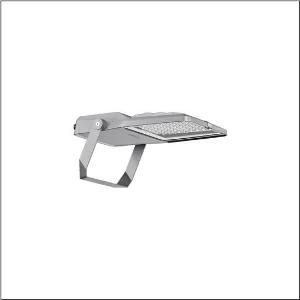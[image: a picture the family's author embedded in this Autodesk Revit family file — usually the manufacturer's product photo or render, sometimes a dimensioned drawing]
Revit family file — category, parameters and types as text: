
# Revit family: floodlight_fl_21_mini___pl64_5xa7775d2e1a_23e2
name_source: partatom
category: Lighting Fixtures
units: mm (PartAtom-declared; Revit-internal decimal feet)

## family parameters
Cut with Voids When Loaded = No
Host = Face
Light Source = No
Part Type = Normal
Room Calculation Point = No
Round Connector Dimension = Use Diameter
Shared = No

## types (1)
- --- (1 x LED, 17220 lm, 142.9 W, 3000K)
    Apparent Load = 143 VA
    CIE Flux Codes = 28 80 98 100 100
    Color Rendering = 70
    Color Temperature = 3000K
    Default Elevation = 1800 mm
    Description = Floodlight FL 21 mini, floodlight, primary light control with lens, of PMMA, primary optical cover: protective disc, of toughened safety glass, transparent, light distribution: PL64, light emission: direct distribution, installation type: surface-mounted, LED, High Power LED, rated luminous flux: 17.220lm, luminous efficacy: 121lm/W, light colour: 730, colour temperature: 3000K, control: flexible luminous flux parameterisation, time-dependent luminous flux control, constant luminous flux control, overheat protection, presetting dimming logarithmic, with terminal, 6-pole, mains connection: 220..240V, AC, 50/60Hz, start of lifetime: 143W, end of service life: 151W, reduction: 63W, luminaire housing, of diecast aluminium, powder-coated, Siteco® metallic grey (DB 702S), corrosivity category C5 mid according to DIN EN ISO 12944, sealing non-destructively replaceable, mounting bracket, of steel, galvanised, powder-coated, Siteco® metallic grey (DB 702S), Smart Interface above, protection rating (complete): IP66, insulation class (complete): insulation class II (safety insulation), certification: CE, ENEC, VDE, protection symbol: D, impact resistance: IK08, permissible operating ambient temperature: -40..+40°C, permissible operating ambient temperature for outdoor applications: -40..+50°C, standard: DIN EN 12944, LABS conformity tested according to VDMA 24364:2018-05, packaging unit: 1 piece

Light Distribution: PL64
    Height = 70 mm
    Lamp = 1 x LED
    Lamp Light Flux = 17220 lm
    Lamp Power = 142.9 W
    Lamp count = 1
    Length = 485 mm
    Luminous efficacy = 121 lm/W
    Manufacturer = Siteco
    ModVariant = No
    Model = 5XA7775D2E1A
    Number of Poles = 1
    OnlyDefault = Yes
    Power Factor = 1
    Product Name = Floodlight FL 21 mini | PL64
    Product group = floodlight | pylon annexe
    ProductGroupID = 6200
    Protection Class = Protection class II
    Protection Degree = IP 66
    RLX_Detail_Level = 1
    RLX_Emergency_Light_Flux = 0 lm
    RLX_Emergency_Type = 0
    RLX_Emergency_Type_DB = No
    RlxData = <blob elided: 96225 chars, md5=71c82e02>
    Socket = socket
    Standby Power = 0 W
    System Light Flux = 17220 lm
    System Power = 143 W
    Type Comments = factory setting: luminous flux: 100 % | dim-lin: 254 | 730 mA
    Type Image = l_1006845.jpg
    URL = http://relux.com
    VarID = @adj_097611
    Voltage = 0 V
    Weight = 0.00 kg
    Width = 337 mm

## geometry (parser evidence)
native form markers: Blend x4, Sweep x11
no freeform markers — native parametric forms only
